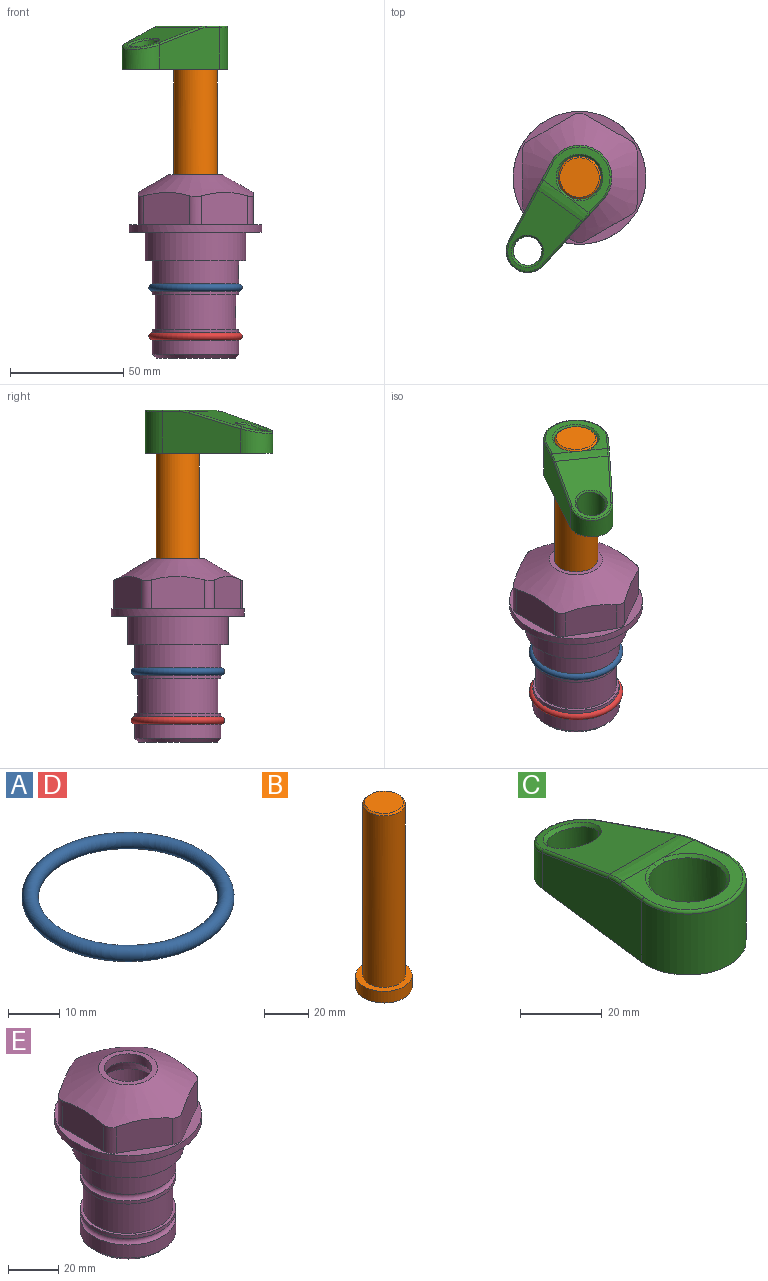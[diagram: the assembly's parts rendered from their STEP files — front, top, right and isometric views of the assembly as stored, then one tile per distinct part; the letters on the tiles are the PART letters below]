
ASSEMBLY  parts=5 mates=4
PART A: 1 faces, bbox 44.7x44.7x3.2 mm
  f0: torus R=19.05mm, axis (0,0,1), area 1193.9mm2
PART B: 6 faces, bbox 25.4x25.4x101.6 mm
  f0: plane 17.46x17.46mm, normal (0,0,1), area 239.5mm2, adj f5
  f1: plane 25.4x25.4mm, normal (0,0,-1), area 506.7mm2, adj f2
  f2: cylinder r=12.7mm len=25.4mm, axis (0,0,1), area 506.7mm2, adj f1,f3
  f3: plane 25.4x25.4mm, normal (0,0,1), area 221.7mm2, adj f2,f4
  f4: cylinder r=9.53mm len=94.46mm, axis (0,0,1), area 5653mm2, adj f3,f5
  f5: cone r=8.73mm half-angle=45deg, axis (0,0,-1), area 64.4mm2, adj f0,f4
PART C: 31 faces, bbox 31.7x65.5x19.8 mm
  f0: plane 39.12x18.26mm, normal (0.99,0.12,0), area 612.2mm2, adj f1,f4,f7,f11,f13,f15
  f1: cylinder r=9.53mm len=18.91mm, axis (0,0,-1), area 296.1mm2, adj f0,f2,f7,f17
  f2: plane 39.12x18.26mm, normal (-0.99,0.12,0), area 612.2mm2, adj f1,f4,f7,f12,f14,f16
  f3: cylinder r=6.35mm len=12.7mm, axis (0,0,-1), area 362.4mm2, adj f7,f18
  f4: cylinder r=14.29mm len=28.58mm, axis (0,0,-1), area 882.2mm2, adj f0,f2,f7,f10
  f5: cylinder r=9.53mm len=19.05mm, axis (0,0,-1), area 1092.6mm2, adj f7,f19,f20
  f6: plane 26.99x23.69mm, normal (0,0,1), area 216.2mm2, adj f9,f10,f11,f12,f19
  f7: plane 63.5x28.58mm, normal (0,0,-1), area 661.8mm2, adj f0,f1,f2,f3,f4,f5,f22,f23
  f8: plane 33.52x23.6mm, normal (0,0.26,0.97), area 486mm2, adj f9,f15,f16,f17,f18
  f9: cylinder r=19.05mm len=24.72mm, axis (1,0,0), area 120.4mm2, adj f6,f8,f13,f14,f20
  f10: torus R=13.49mm, axis (0,0,1), area 59mm2, adj f4,f6,f11,f12
  f11: cylinder r=0.79mm len=8.67mm, axis (0.12,-0.99,0), area 10.8mm2, adj f0,f6,f10,f13
  f12: cylinder r=0.79mm len=8.67mm, axis (0.12,0.99,0), area 10.8mm2, adj f2,f6,f10,f14
  f13: bspline ~4.95x1.42mm, area 6.1mm2, adj f0,f9,f11,f15
  f14: bspline ~4.95x1.42mm, area 6.1mm2, adj f2,f9,f12,f16
  f15: cylinder r=0.79mm len=25.95mm, axis (0.12,-0.96,0.26), area 32.9mm2, adj f0,f8,f13,f17
  f16: cylinder r=0.79mm len=25.95mm, axis (0.12,0.96,-0.26), area 32.9mm2, adj f2,f8,f14,f17
  f17: bspline ~18.91x8.38mm, area 30mm2, adj f1,f8,f15,f16
  f18: bspline ~14.29x14.29mm, area 48.3mm2, adj f3,f8
  f19: cone r=9.53mm half-angle=45deg, axis (0,0,1), area 66.5mm2, adj f5,f6,f20
  f20: bspline ~3.22x0.96mm, area 3.5mm2, adj f5,f9,f19
  f21: plane 2.75x2.72mm, normal (0,0,-1), area 2.9mm2, adj f23,f25,f28
  f22: plane 23.05x15.88mm, normal (-0.99,-0.12,0), area 323.6mm2, adj f7,f25,f26,f27,f28,f29
  f23: plane 23.05x15.88mm, normal (0.99,-0.12,0), area 323.6mm2, adj f7,f21,f25,f27,f28,f30
  f24: cylinder r=9.53mm len=10.69mm, axis (0,0,-1), area 114.7mm2, adj f7,f27,f29,f30
  f25: cylinder r=12.7mm len=20.59mm, axis (0,0,-1), area 381.1mm2, adj f7,f21,f22,f23,f26,f28
  f26: plane 2.75x2.72mm, normal (0,0,-1), area 2.9mm2, adj f22,f25,f28
  f27: plane 19.72x18.37mm, normal (0,-0.26,-0.97), area 291.8mm2, adj f22,f23,f24,f28,f29,f30
  f28: cylinder r=15.88mm len=19.92mm, axis (1,0,0), area 54.8mm2, adj f21,f22,f23,f25,f26,f27
  f29: cylinder r=1.59mm len=11mm, axis (0,0,-1), area 34.7mm2, adj f7,f22,f24,f27
  f30: cylinder r=1.59mm len=11mm, axis (0,0,-1), area 34.7mm2, adj f7,f23,f24,f27
PART D: same geometry as A
PART E: 36 faces, bbox 58.7x58.7x81 mm
  f0: cylinder r=17.78mm len=35.56mm, axis (0,0,1), area 1670.8mm2, adj f23,f24,f31
  f1: cylinder r=19.05mm len=38.1mm, axis (0,0,1), area 1191.9mm2, adj f26,f27,f30
  f2: plane 58.66x58.66mm, normal (0,0,-1), area 1150.6mm2, adj f3,f28
  f3: cylinder r=29.33mm len=58.66mm, axis (0,0,-1), area 585.1mm2, adj f2,f4
  f4: plane 58.66x58.66mm, normal (0,0,1), area 475.9mm2, adj f3,f5,f6,f7,f8,f9,f10,f11
  f5: plane 20.32x14.34mm, normal (-0.5,0.87,0), area 324.4mm2, adj f4,f15,f16,f17
  f6: plane 20.32x14.34mm, normal (0.5,0.87,0), area 324.4mm2, adj f4,f14,f15,f17
  f7: plane 23.48x14.34mm, normal (1,0,0), area 324.4mm2, adj f4,f13,f14,f17
  f8: plane 20.32x14.34mm, normal (0.5,-0.87,0), area 324.4mm2, adj f4,f12,f13,f17
  f9: plane 20.32x14.34mm, normal (-0.5,-0.87,0), area 324.4mm2, adj f4,f11,f12,f17
  f10: plane 23.48x14.34mm, normal (-1,0,0), area 324.4mm2, adj f4,f11,f16,f17
  f11: cylinder r=5.08mm len=12.85mm, axis (0,0,-1), area 67.2mm2, adj f4,f9,f10,f17
  f12: cylinder r=5.08mm len=12.85mm, axis (0,0,-1), area 67.2mm2, adj f4,f8,f9,f17
  f13: cylinder r=5.08mm len=12.85mm, axis (0,0,-1), area 67.2mm2, adj f4,f7,f8,f17
  f14: cylinder r=5.08mm len=12.85mm, axis (0,0,-1), area 67.2mm2, adj f4,f6,f7,f17
  f15: cylinder r=5.08mm len=12.85mm, axis (0,0,-1), area 67.2mm2, adj f4,f5,f6,f17
  f16: cylinder r=5.08mm len=12.85mm, axis (0,0,-1), area 67.2mm2, adj f4,f5,f10,f17
  f17: cone r=11.73mm half-angle=60deg, axis (0,0,-1), area 2071.8mm2, adj f5,f6,f7,f8,f9,f10,f11,f12
  f18: plane 23.46x23.46mm, normal (0,0,1), area 147.4mm2, adj f17,f35
  f19: plane 34.93x34.93mm, normal (0,0,-1), area 958mm2, adj f29
  f20: cylinder r=19.05mm len=38.1mm, axis (0,0,1), area 760.1mm2, adj f21,f29
  f21: torus R=19.05mm, axis (0,0,1), area 565.3mm2, adj f20,f22
  f22: cylinder r=19.05mm len=38.1mm, axis (0,0,1), area 190mm2, adj f21,f23
  f23: plane 38.1x38.1mm, normal (0,0,1), area 146.9mm2, adj f0,f22
  f24: plane 38.1x38.1mm, normal (0,0,-1), area 146.9mm2, adj f0,f25
  f25: cylinder r=19.05mm len=38.1mm, axis (0,0,1), area 190mm2, adj f24,f26
  f26: torus R=19.05mm, axis (0,0,1), area 565.3mm2, adj f1,f25
  f27: plane 44.45x44.45mm, normal (0,0,-1), area 411.7mm2, adj f1,f28
  f28: cylinder r=22.23mm len=44.45mm, axis (0,0,1), area 1773.5mm2, adj f2,f27
  f29: cone r=19.05mm half-angle=45deg, axis (0,0,1), area 257.5mm2, adj f19,f20
  f30: cylinder r=3.17mm len=6.75mm, axis (-1,0,0), area 128mm2, adj f1,f33
  f31: cylinder r=3.17mm len=6.35mm, axis (-1,0,0), area 102.5mm2, adj f0,f33
  f32: plane 25.4x25.4mm, normal (0,0,1), area 506.7mm2, adj f33
  f33: cylinder r=12.7mm len=66.42mm, axis (0,0,-1), area 5236.2mm2, adj f30,f31,f32,f34
  f34: cone r=9.53mm half-angle=30deg, axis (0,0,-1), area 443.4mm2, adj f33,f35
  f35: cylinder r=9.53mm len=19.05mm, axis (0,0,-1), area 240.9mm2, adj f18,f34
PLACE A at identity
PLACE B rot(axis=(0,0,1),144.7deg) t=(0,0,27.55)mm
PLACE C rot(axis=(0,0,1),144.7deg) t=(0,0,27.55)mm
PLACE D t=(0,0,-21.59)mm
PLACE E at identity fixed
MATE fastened B.f2 <-> C.f4  axis (0,0,1) through (0,0,91.05)mm
MATE cylindrical B.f2 <-> E.f0  axis (0,0,-1) through (0,0,-10.55)mm
MATE fastened A.f0 <-> E.f0  axis (0,0,1) through (0,0,-24.51)mm
MATE fastened D.f0 <-> E.f0  axis (0,0,1) through (0,0,-46.1)mm
